# Revit family: rba-bim-rba1083-series
name_source: partatom
category: Plumbing Fixtures
revit_build: Autodesk Revit 2016 (Build: 20151007_0715(x64)
units: mm (PartAtom-declared; Revit-internal decimal feet)

## family parameters
Always vertical = Yes
Cut with Voids When Loaded = No
Part Type = Normal
Room Calculation Point = No
Round Connector Dimension = Use Diameter
Shared = No
Work Plane-Based = Yes

## types (6) — shared parameters
Default Elevation = 1219 mm
URL = www.rba.com.au

## per-type parameters (varying)
| type | Description | Manufacturer | Tap | Tap Head Polished | Tap Head Satin |
| RBA1083-650 | 6 Star WELS, 1.7Lpm | DOCOL | Bright Polished Stainless Steel | Yes | No |
| RBA1083-657 | 6 Star WELS, 1.7Lpm | rba | Satin Stainless Steel | No | Yes |
| RBA1083-600 | 6 Star WELS, 5.0Lpm | rba | Bright Polished Stainless Steel | Yes | No |
| RBA1083-607 | 6 Star WELS, 5.0Lpm | rba | Satin Stainless Steel | No | Yes |
| RBA1083-400 | 4 Star WELS, 8.0Lpm | rba | Bright Polished Stainless Steel | Yes | No |
| RBA1083-407 | 4 Star WELS, 8.0Lpm | rba | Satin Stainless Steel | No | Yes |

note: column(s) folded — value = type name in every type: Model

## geometry (parser evidence)
native form markers: Blend x14, Sweep x2
no freeform markers — native parametric forms only
